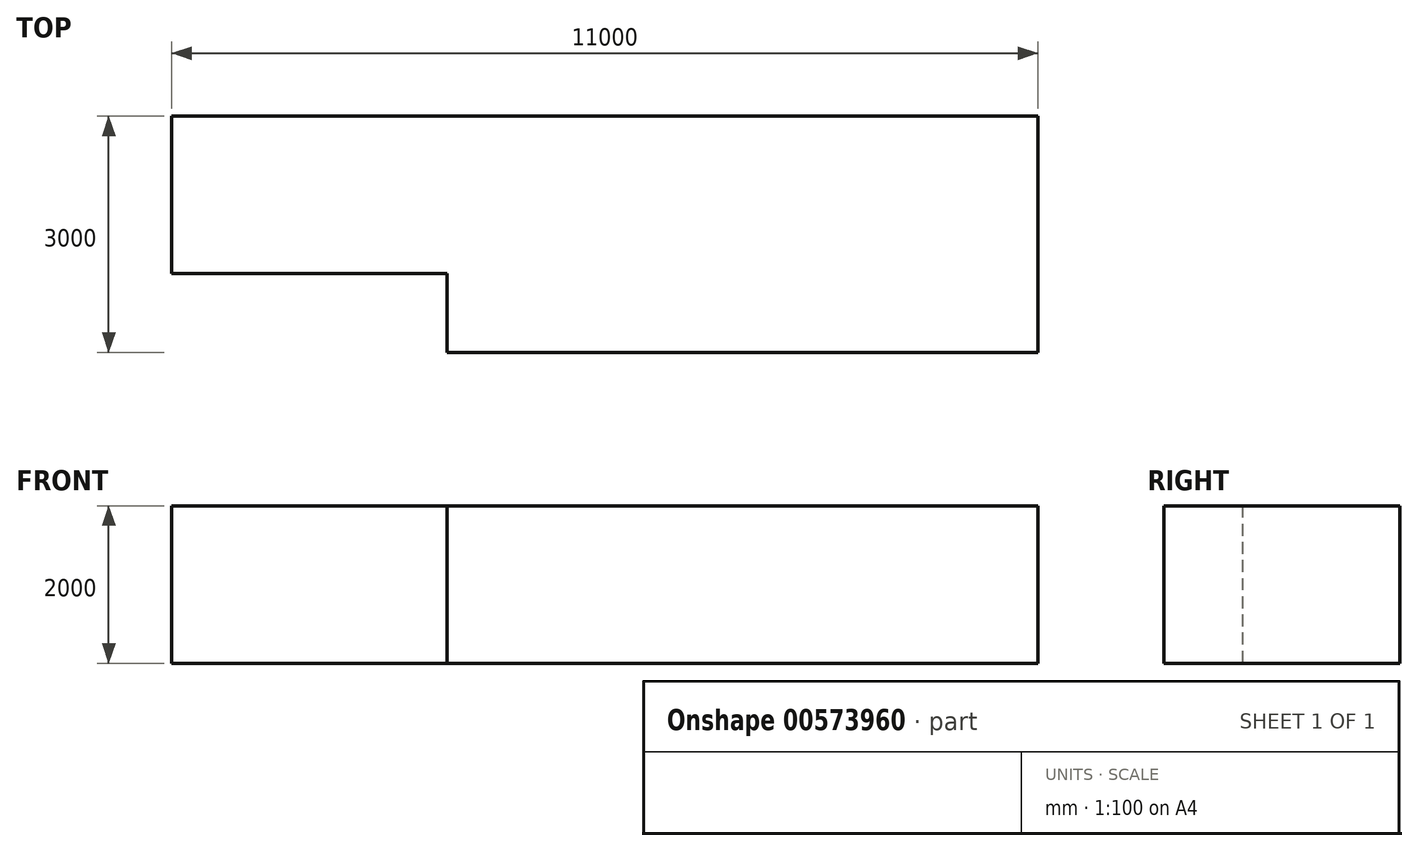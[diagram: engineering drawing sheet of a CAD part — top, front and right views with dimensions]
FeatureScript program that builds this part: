
annotation { "Feature Type Name" : "Feature", "Feature Type Description" : "" }
export const myFeature = defineFeature(function(context is Context, id is Id, definition is map)
    precondition{}
    {
        {
            var Q0;
            Q0=qCreatedBy(makeId("Top.planeOp"),FACE);
            var sketch = newSketch(context, id + "F0", { "sketchPlane" : qUnion([Q0])});
            skLineSegment(sketch, "E0.bottom", {"start": v(5500, 1500) * mm, "end": v(-5500, 1500) * mm});
            skLineSegment(sketch, "E0.left", {"start": v(5500, 1500) * mm, "end": v(5500, -1500) * mm});
            skPoint(sketch, "E0.middle", {"position": v(0, 0) * mm});
            skLineSegment(sketch, "E1.top", {"start": v(-5500, -500) * mm, "end": v(-2000, -500) * mm});
            skLineSegment(sketch, "E1.right", {"start": v(-2000, -1500) * mm, "end": v(-2000, -500) * mm});
            skLineSegment(sketch, "E2", {"start": v(-5500, 1500) * mm, "end": v(-5500, -500) * mm});
            skLineSegment(sketch, "E3", {"start": v(-2000, -1500) * mm, "end": v(5500, -1500) * mm});
            skSolve(sketch);
        }
        {
            var Q0;
            Q0 = qSketchRegion(id + "F0", true);
            extrude(context, id + "F1", {"entities" : qUnion([Q0]), "depth" : 2000 * mm, "offsetDistance" : 25 * mm});
        }
    });
